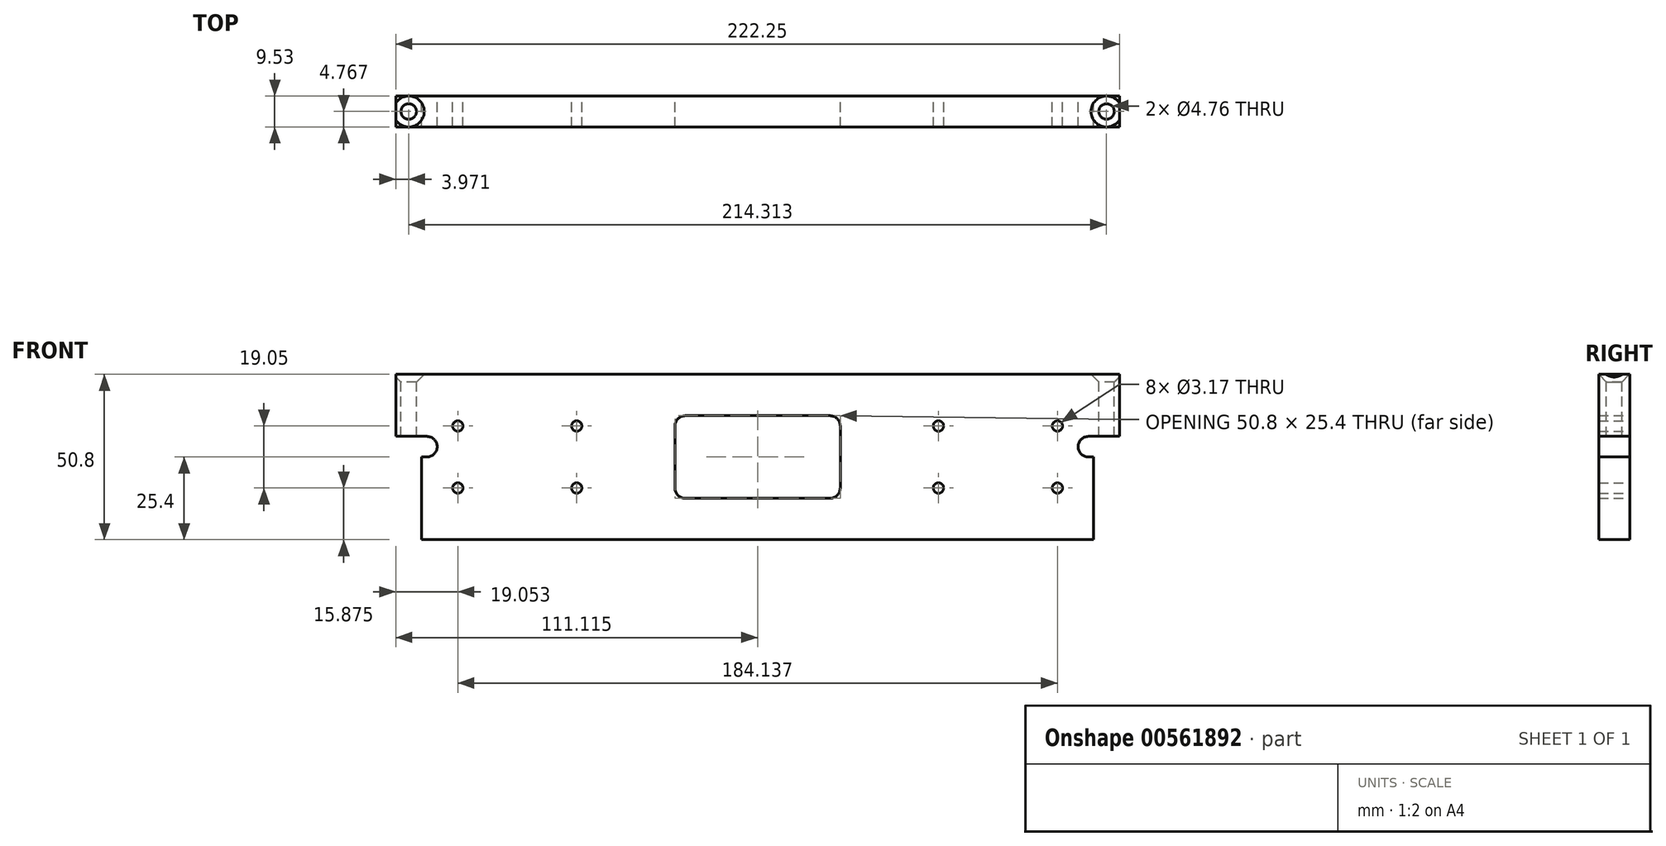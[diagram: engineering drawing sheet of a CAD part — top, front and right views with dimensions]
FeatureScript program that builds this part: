
annotation { "Feature Type Name" : "Feature", "Feature Type Description" : "" }
export const myFeature = defineFeature(function(context is Context, id is Id, definition is map)
    precondition{}
    {
        {
            var Q0;
            Q0=qCreatedBy(makeId("Front.planeOp"),FACE);
            var sketch = newSketch(context, id + "F0", { "sketchPlane" : qUnion([Q0])});
            skLineSegment(sketch, "E0", {"start": v(0, 0) * mm, "end": v(206.38, 0) * mm});
            skLineSegment(sketch, "E1", {"start": v(206.38, 50.8) * mm, "end": v(0, 50.8) * mm});
            skLineSegment(sketch, "E2", {"start": v(0, 50.8) * mm, "end": v(-7.94, 50.8) * mm});
            skLineSegment(sketch, "E3", {"start": v(-7.94, 50.8) * mm, "end": v(-7.94, 31.75) * mm});
            skLineSegment(sketch, "E4", {"start": v(-7.94, 31.75) * mm, "end": v(0, 31.75) * mm});
            skLineSegment(sketch, "E5", {"start": v(0, 31.75) * mm, "end": v(0, 0) * mm});
            skLineSegment(sketch, "E6", {"start": v(214.31, 50.8) * mm, "end": v(214.31, 31.75) * mm});
            skLineSegment(sketch, "E7", {"start": v(214.31, 31.75) * mm, "end": v(206.38, 31.75) * mm});
            skLineSegment(sketch, "E8", {"start": v(206.38, 31.75) * mm, "end": v(206.38, 0) * mm});
            skLineSegment(sketch, "E9", {"start": v(3.17, 50.8) * mm, "end": v(3.17, 0) * mm, "construction": true});
            skLineSegment(sketch, "E10", {"start": v(11.11, 50.8) * mm, "end": v(11.11, 0) * mm, "construction": true});
            skLineSegment(sketch, "E11", {"start": v(47.62, 50.8) * mm, "end": v(47.62, 0) * mm, "construction": true});
            skLineSegment(sketch, "E12", {"start": v(11.11, 15.87) * mm, "end": v(47.62, 15.88) * mm, "construction": true});
            skLineSegment(sketch, "E13", {"start": v(11.11, 34.92) * mm, "end": v(47.62, 34.92) * mm, "construction": true});
            skCircle(sketch, "E14", {"center": v(11.11, 34.92) * mm, "radius": 1.59 * mm});
            skCircle(sketch, "E15", {"center": v(11.11, 15.87) * mm, "radius": 1.59 * mm});
            skCircle(sketch, "E16", {"center": v(47.62, 34.93) * mm, "radius": 1.59 * mm});
            skCircle(sketch, "E17", {"center": v(47.62, 15.88) * mm, "radius": 1.59 * mm});
            skLineSegment(sketch, "E18", {"start": v(203.2, 50.8) * mm, "end": v(203.2, 0) * mm, "construction": true});
            skLineSegment(sketch, "E19", {"start": v(195.25, 50.8) * mm, "end": v(195.25, 0) * mm, "construction": true});
            skLineSegment(sketch, "E20", {"start": v(158.72, 50.8) * mm, "end": v(158.72, 0) * mm, "construction": true});
            skLineSegment(sketch, "E21", {"start": v(158.72, 34.93) * mm, "end": v(195.25, 34.93) * mm, "construction": true});
            skLineSegment(sketch, "E22", {"start": v(158.72, 15.87) * mm, "end": v(195.25, 15.88) * mm, "construction": true});
            skCircle(sketch, "E23", {"center": v(158.72, 34.93) * mm, "radius": 1.59 * mm});
            skCircle(sketch, "E24", {"center": v(195.25, 34.93) * mm, "radius": 1.59 * mm});
            skCircle(sketch, "E25", {"center": v(195.25, 15.88) * mm, "radius": 1.59 * mm});
            skCircle(sketch, "E26", {"center": v(158.72, 15.87) * mm, "radius": 1.59 * mm});
            skLineSegment(sketch, "E27.bottom", {"start": v(77.77, 38.1) * mm, "end": v(128.57, 38.1) * mm});
            skLineSegment(sketch, "E27.top", {"start": v(77.77, 12.7) * mm, "end": v(128.57, 12.7) * mm});
            skLineSegment(sketch, "E27.left", {"start": v(77.77, 38.1) * mm, "end": v(77.77, 12.7) * mm});
            skLineSegment(sketch, "E27.right", {"start": v(128.57, 38.1) * mm, "end": v(128.57, 12.7) * mm});
            skLineSegment(sketch, "E28", {"start": v(128.57, 38.1) * mm, "end": v(158.72, 50.8) * mm, "construction": true});
            skLineSegment(sketch, "E29", {"start": v(128.57, 12.7) * mm, "end": v(158.72, 0) * mm, "construction": true});
            skLineSegment(sketch, "E30", {"start": v(77.77, 12.7) * mm, "end": v(47.62, 0) * mm, "construction": true});
            skLineSegment(sketch, "E31", {"start": v(77.77, 38.1) * mm, "end": v(47.62, 50.8) * mm, "construction": true});
            skLineSegment(sketch, "E32", {"start": v(206.38, 50.8) * mm, "end": v(214.31, 50.8) * mm});
            skCircle(sketch, "E33", {"center": v(204.79, 28.58) * mm, "radius": 3.18 * mm});
            skCircle(sketch, "E34", {"center": v(1.59, 28.57) * mm, "radius": 3.18 * mm});
            skLineSegment(sketch, "E35", {"start": v(206.38, 31.75) * mm, "end": v(204.79, 31.75) * mm});
            skLineSegment(sketch, "E36", {"start": v(206.38, 25.4) * mm, "end": v(204.79, 25.4) * mm});
            skLineSegment(sketch, "E37", {"start": v(0, 31.75) * mm, "end": v(1.59, 31.75) * mm});
            skLineSegment(sketch, "E38", {"start": v(0, 25.4) * mm, "end": v(1.59, 25.4) * mm});
            skSolve(sketch);
        }
        {
            var Q0;
            {var subQ2=sQuery(id+"F0.wireOp",EDGE,"E0");Q0=makeQuery(id+"F0.imprint","IMPRINT",FACE,{"disambiguationData":[TD([[makeQuery(id+"F0.imprint","IMPRINT",EDGE,{"derivedFrom":subQ2}),1.0]])]});}
            extrude(context, id + "F1", {"entities" : qUnion([Q0]), "depth" : 9.52 * mm, "offsetDistance" : 25.4 * mm});
        }
        {
            var Q0;
            Q0=makeQuery(id+"F1.opExtrude","SWEPT_EDGE",EDGE,{"disambiguationData":[OSD([sQuery(id+"F0.wireOp",EDGE,"E27.top"),sQuery(id+"F0.wireOp",EDGE,"E27.left")])]});
            var Q1;
            Q1=makeQuery(id+"F1.opExtrude","SWEPT_EDGE",EDGE,{"disambiguationData":[OSD([sQuery(id+"F0.wireOp",EDGE,"E27.top"),sQuery(id+"F0.wireOp",EDGE,"E27.right")])]});
            var Q2;
            Q2=makeQuery(id+"F1.opExtrude","SWEPT_EDGE",EDGE,{"disambiguationData":[OSD([sQuery(id+"F0.wireOp",EDGE,"E27.bottom"),sQuery(id+"F0.wireOp",EDGE,"E27.left")])]});
            var Q3;
            Q3=makeQuery(id+"F1.opExtrude","SWEPT_EDGE",EDGE,{"disambiguationData":[OSD([sQuery(id+"F0.wireOp",EDGE,"E27.bottom"),sQuery(id+"F0.wireOp",EDGE,"E27.right")])]});
            fillet(context, id + "F2", {"entities" : qUnion([Q0, Q1, Q2, Q3]), "radius" : 3.17 * mm, "tangentPropagation" : true, "allowEdgeOverflow" : false});
        }
        {
            var Q0;
            Q0=makeQuery(id+"F1.opExtrude","SWEPT_FACE",FACE,{"disambiguationData":[OSD([sQuery(id+"F0.wireOp",EDGE,"E1"),sQuery(id+"F0.wireOp",EDGE,"E2"),sQuery(id+"F0.wireOp",EDGE,"E32")])]});
            var sketch = newSketch(context, id + "F3", { "sketchPlane" : qUnion([Q0])});
            skLineSegment(sketch, "E39", {"start": v(-3.97, 0) * mm, "end": v(-3.97, -9.53) * mm, "construction": true});
            skLineSegment(sketch, "E40", {"start": v(210.34, 0) * mm, "end": v(210.34, -9.53) * mm, "construction": true});
            skPoint(sketch, "E41", {"position": v(210.34, -4.76) * mm});
            skPoint(sketch, "E42", {"position": v(-3.97, -4.76) * mm});
            skSolve(sketch);
        }
        {
            var Q0;
            Q0=sQuery(id+"F3.wireOp",VERTEX,"E42");
            var Q1;
            Q1=sQuery(id+"F3.wireOp",VERTEX,"E41");
            var Q2;
            Q2=makeQuery(id+"F1.opExtrude","SWEPT_BODY",BODY,{"disambiguationData":[OSD([sQuery(id+"F0.wireOp",EDGE,"E0"),sQuery(id+"F0.wireOp",EDGE,"E1"),sQuery(id+"F0.wireOp",EDGE,"E2"),sQuery(id+"F0.wireOp",EDGE,"E3"),sQuery(id+"F0.wireOp",EDGE,"E4"),sQuery(id+"F0.wireOp",EDGE,"E5"),sQuery(id+"F0.wireOp",EDGE,"E6"),sQuery(id+"F0.wireOp",EDGE,"E7"),sQuery(id+"F0.wireOp",EDGE,"E8"),sQuery(id+"F0.wireOp",EDGE,"E14"),sQuery(id+"F0.wireOp",EDGE,"E15"),sQuery(id+"F0.wireOp",EDGE,"E16"),sQuery(id+"F0.wireOp",EDGE,"E17"),sQuery(id+"F0.wireOp",EDGE,"E23"),sQuery(id+"F0.wireOp",EDGE,"E24"),sQuery(id+"F0.wireOp",EDGE,"E25"),sQuery(id+"F0.wireOp",EDGE,"E26"),sQuery(id+"F0.wireOp",EDGE,"PPNb4jjt-c5Pm-yymI-Qylr-i9J2qvPI4Ybe"),sQuery(id+"F0.wireOp",EDGE,"vq8NmP2y-PkYv-aiXb-gz1U-ERsO9vgSuKFc"),sQuery(id+"F0.wireOp",EDGE,"E27.bottom"),sQuery(id+"F0.wireOp",EDGE,"E27.top"),sQuery(id+"F0.wireOp",EDGE,"E27.left"),sQuery(id+"F0.wireOp",EDGE,"E27.right"),sQuery(id+"F0.wireOp",EDGE,"E32")])]});
            hole(context, id + "F4", {"style" : HoleStyle.C_SINK, "endStyle" : HoleEndStyle.THROUGH, "holeDiameter" : 4.76 * mm, "cSinkDiameter" : 9.52 * mm, "cSinkAngle" : 90 * degree, "majorDiameter" : 6.35 * mm, "isTappedThrough" : true, "tappedDepth" : 12.7 * mm, "tapClearance" : 3, "startFromSketch" : true, "locations" : qUnion([Q0, Q1]), "scope" : qUnion([Q2])});
        }
    });
